# Revit family: Reece_Bath_Kado_Lussi_Freestanding Bath_Cast Solid Surface_1505 mm
name_source: partatom
category: Plumbing Fixtures
revit_build: Autodesk Revit 2018 (Build: 20190510_1515(x64)
units: mm (PartAtom-declared; Revit-internal decimal feet)

## family parameters
Always vertical = Yes
Cut with Voids When Loaded = Yes
Part Type = Normal
Room Calculation Point = Yes
Round Connector Dimension = Use Diameter
Shared = Yes
Work Plane-Based = Yes

## types (1)
- 1505 mm_267 ltr_White
    Default Elevation = 0 mm  [stored 0 ft]
    Description = Kado Lussi Cast Solid Surface Freestanding Bath with Plug & Waste 1500mm
    Disclaimer = THIS FILE IS THE PROPERTY OF THE REECE GROUP. IT MAY NOT BE REPRODUCED, REVERSE-ENGINEERED OR MODIFIED. ANY REPUBLICATION, TRANSMISSION OR DISTRIBUTION FOR THE PURPOSE OF COMMERCIALLY EXPLOITING THE FILES IS PROHIBITED.
    Keynote = Product #9506953, Reece_Bath_Kado_Lussi_Freestanding Bath_Cast Solid Surface_1505 mm - 1505 mm_267 ltr_White
    Manufacturer = Kado
    Model = Lussi
    Reece_Bath_Outlet = 40 mm  [stored 0.131234 ft]
    Reece_Detail_Connector = Bottom Inlet
    Reece_Detail_Disclaimer = THIS FILE IS THE PROPERTY OF THE REECE GROUP. IT MAY NOT BE REPRODUCED, REVERSE-ENGINEERED OR MODIFIED. ANY REPUBLICATION, TRANSMISSION OR DISTRIBUTION FOR THE PURPOSE OF COMMERCIALLY EXPLOITING THE FILES IS PROHIBITED.
    Reece_Detail_Installation = Freestanding Bath
    Reece_Material_Main = Reece_Cast_Solid_Surface_White
    Reece_Overall_Capacity = 267 L
    Reece_Overall_Height = 570 mm  [stored 1.87008 ft]
    Reece_Overall_Length = 1505 mm  [stored 4.93766 ft]
    Reece_Overall_Width = 730 mm  [stored 2.39501 ft]
    Reece_Product_Brand = Kado
    Reece_Product_Description = Kado Lussi Cast Solid Surface Freestanding Bath with Plug & Waste 1500mm
    Reece_Product_Mount = Floor Mounted
    Reece_Product_Number = 9506953
    Reece_Product_Sub Brand = Lussi
    Reece_Product_Type = Bath
    Reece_Product_Web Page = https://www.reece.com.au
    Type Comments = Bath
    URL = https://www.reece.com.au

note: [stored X ft] marks values corroborated as IEEE doubles in the binary element streams (Revit-internal decimal feet)

## geometry (parser evidence)
native form markers: Sweep x6
no freeform markers — native parametric forms only
